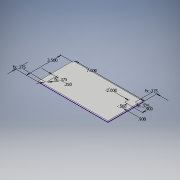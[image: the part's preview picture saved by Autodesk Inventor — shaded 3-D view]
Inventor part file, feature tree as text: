
AUTODESK INVENTOR PART (.ipt)
format: ipt  version: 2018 (Build 220112000, 112)  size: 117,248 bytes
history: native  units: in
note: dims shown in document units (in); Inventor stores cm internally (conversion verified against a paired STEP export)
features: sketch x2, extrude x2
ambient origin geometry x8: Origin, YZ Plane, XZ Plane, XY Plane, X Axis, Y Axis, Z Axis, Center Point
bodies: Solid1 (feature_tree)
feature tree (4):
  sketch  "Sketch1"  dims[d0=7.0in d1=3.5in]
  extrude  "Extrusion1"  Depth=3.5in
  extrude  "Extrusion2"  Depth=0.9in
  sketch  "Sketch2"  dims[d2=0.9in d3=0.9in d4=0.5in d5=2.0in d6=0.125in d7=0.0in d8=0.6in d9=0.0in d10=0.375in d11=0.375in d12=0.375in d13=0.375in d14=0.25in d15=0.375in d16=0.375in]
